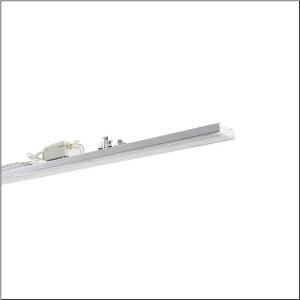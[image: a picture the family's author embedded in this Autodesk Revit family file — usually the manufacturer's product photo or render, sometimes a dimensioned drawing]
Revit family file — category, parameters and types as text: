
# Revit family: licross_21_recessed_mo_52tl10mn4a5g
name_source: partatom
category: Lighting Fixtures
units: mm (PartAtom-declared; Revit-internal decimal feet)

## family parameters
Cut with Voids When Loaded = No
Host = Face
Light Source = No
Part Type = Normal
Room Calculation Point = No
Round Connector Dimension = Use Diameter
Shared = No

## types (1)
- --- (1 x LED, 10690 lm, 60.5 W, 4000K)
    Apparent Load = 61 VA
    CIE Flux Codes = 50 81 96 100 100
    Color Rendering = 80
    Color Temperature = 4000K
    Default Elevation = 1800 mm
    Description = Licross 21 Recessed MO, luminaire insert, of sheet steel, galvanised, coil coated, white, length: 1.500mm, width: 66mm, height: 67mm, LED rated luminous flux: 10.690lm, light colour: 840, SDCM (Standard Deviation of Colour Matching)MacAdam ≤ 3 SDCM (initial), control gear: ON/OFF Multilumen, with plug, 3-pole, with phase selection, mains connection: 220..240V, AC, 50/60Hz, rated input power: 61W, internal wiring halogen-free, primary optical cover: cover, of PMMA, light emission: direct distribution, primary light characteristic: symmetric, protection rating (complete): IP40, insulation class (complete): insulation class I (protective earthing), certification: CE, ENEC, VDE, UKCA, protection symbol: D if used in an environment without relevant dust loads with corresponding accessories, impact resistance: IK06, permissible ambient temperature for indoor applications: -35..+40°C, corresponds to IFS (International Featured Standards) requirements for safety and quality in the food industry, reducing of maximum allowable ambient temperature of 5°C with ceiling mounting, LABS conformity tested according to VDMA 24364:2018-05, The light source and the operating device comply with the requirements of the Ecodesign Regulation (EU) 2019/2020 and are replaceable in accordance with this regulation, packaging unit: 1 piece
    Height = 58 mm
    Lamp = 1 x LED
    Lamp Light Flux = 10690 lm
    Lamp Power = 60.5 W
    Lamp count = 1
    Length = 1500 mm
    Luminous efficacy = 177 lm/W
    Manufacturer = Siteco
    ModVariant = No
    Model = 52TL10MN4A5G
    Mounting Place = Ceiling
    Mounting Type = Pendant
    Number of Poles = 1
    OnlyDefault = Yes
    Power Factor = 1
    Product Name = Licross 21 Recessed MO
    Product group = luminaire insert | ceiling pendant
    ProductGroupID = 901
    Protection Class = Protection class I
    Protection Degree = IP 40
    RLX_Detail_Level = 1
    RLX_Emergency_Light_Flux = 0 lm
    RLX_Emergency_Type = 0
    RLX_Emergency_Type_DB = No
    RlxData = <blob elided: 22389 chars, md5=05f78735>
    Socket = socket
    Standby Power = 0 W
    System Light Flux = 10690 lm
    System Power = 61 W
    Type Comments = factory setting: luminous flux: 100 % | (A | C | E) | 140 mA
    Type Image = l_1296930.jpg
    URL = http://relux.com
    VarID = @adj_109583
    Voltage = 0 V
    Weight = 0.00 kg
    Width = 66 mm

## geometry (parser evidence)
native form markers: Blend x4, Sweep x12
no freeform markers — native parametric forms only
